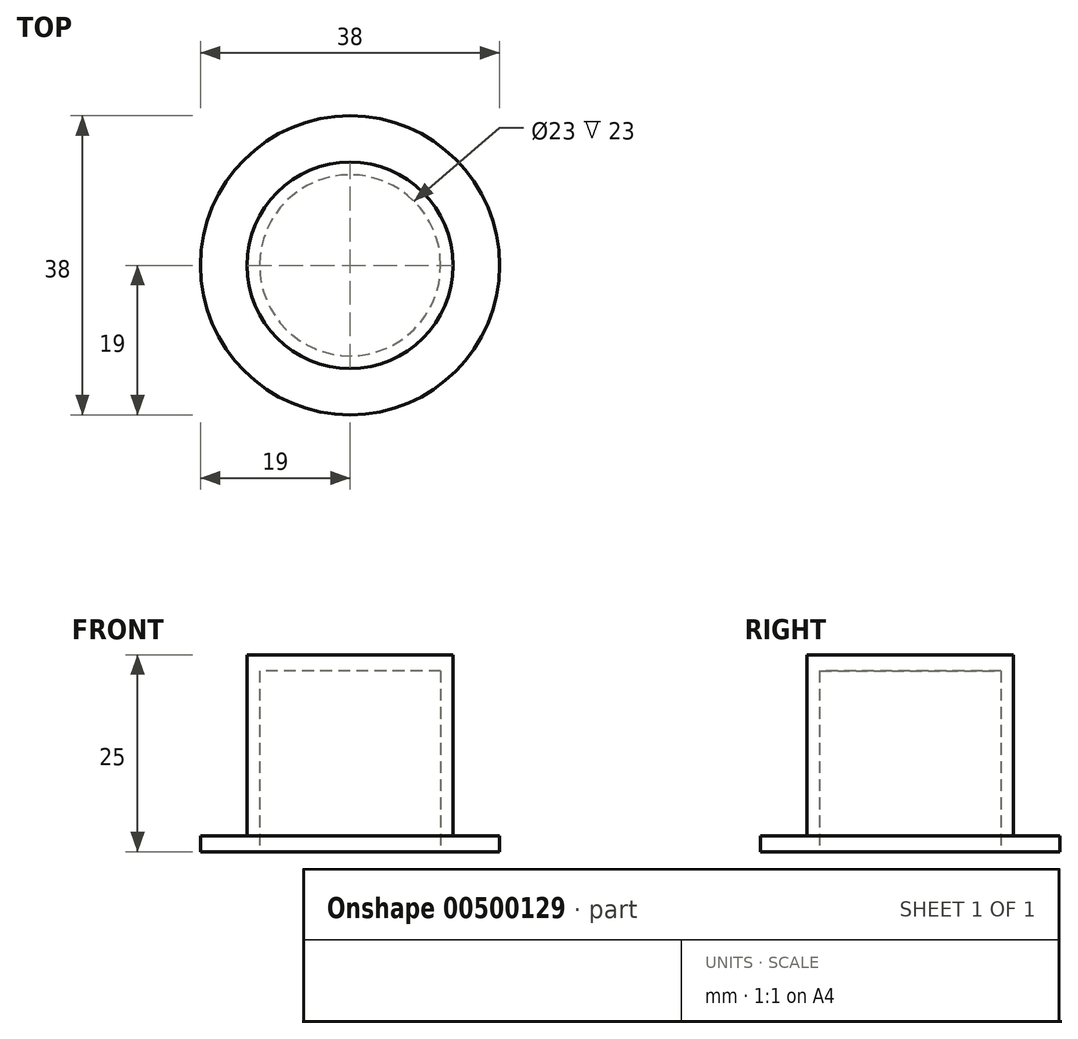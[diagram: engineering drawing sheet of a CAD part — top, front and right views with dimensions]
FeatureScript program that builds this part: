
annotation { "Feature Type Name" : "Feature", "Feature Type Description" : "" }
export const myFeature = defineFeature(function(context is Context, id is Id, definition is map)
    precondition{}
    {
        {
            var Q0;
            Q0=qCreatedBy(makeId("Top.planeOp"),FACE);
            var sketch = newSketch(context, id + "F0", { "sketchPlane" : qUnion([Q0])});
            skCircle(sketch, "E0", {"center": v(0, 0) * mm, "radius": 11.5 * mm});
            skCircle(sketch, "E1", {"center": v(0, 0) * mm, "radius": 19 * mm});
            skCircle(sketch, "E2", {"center": v(0, 0) * mm, "radius": 13.1 * mm});
            skSolve(sketch);
        }
        {
            var Q0;
            Q0=makeQuery(id+"F0.imprint","IMPRINT",FACE,{"disambiguationData":[TD([[makeQuery(id+"F0.imprint","IMPRINT",EDGE,{"derivedFrom":sQuery(id+"F0.wireOp",EDGE,"E0")}),1.0]])]});
            var Q1;
            Q1=makeQuery(id+"F0.imprint","IMPRINT",FACE,{"disambiguationData":[TD([[makeQuery(id+"F0.imprint","IMPRINT",EDGE,{"derivedFrom":sQuery(id+"F0.wireOp",EDGE,"E0")}),-1.0]])]});
            extrude(context, id + "F1", {"entities" : qUnion([Q0, Q1]), "depth" : 25 * mm});
        }
        {
            var Q0;
            Q0 = qSketchRegion(id + "F0", true);
            extrude(context, id + "F2", {"entities" : qUnion([Q0]), "operationType" : NewBodyOperationType.ADD, "depth" : 2 * mm});
        }
        {
            var Q0;
            Q0=makeQuery(id+"F0.imprint","IMPRINT",FACE,{"disambiguationData":[TD([[makeQuery(id+"F0.imprint","IMPRINT",EDGE,{"derivedFrom":sQuery(id+"F0.wireOp",EDGE,"E0")}),1.0]])]});
            extrude(context, id + "F3", {"entities" : qUnion([Q0]), "operationType" : NewBodyOperationType.REMOVE, "depth" : 23 * mm});
        }
    });
